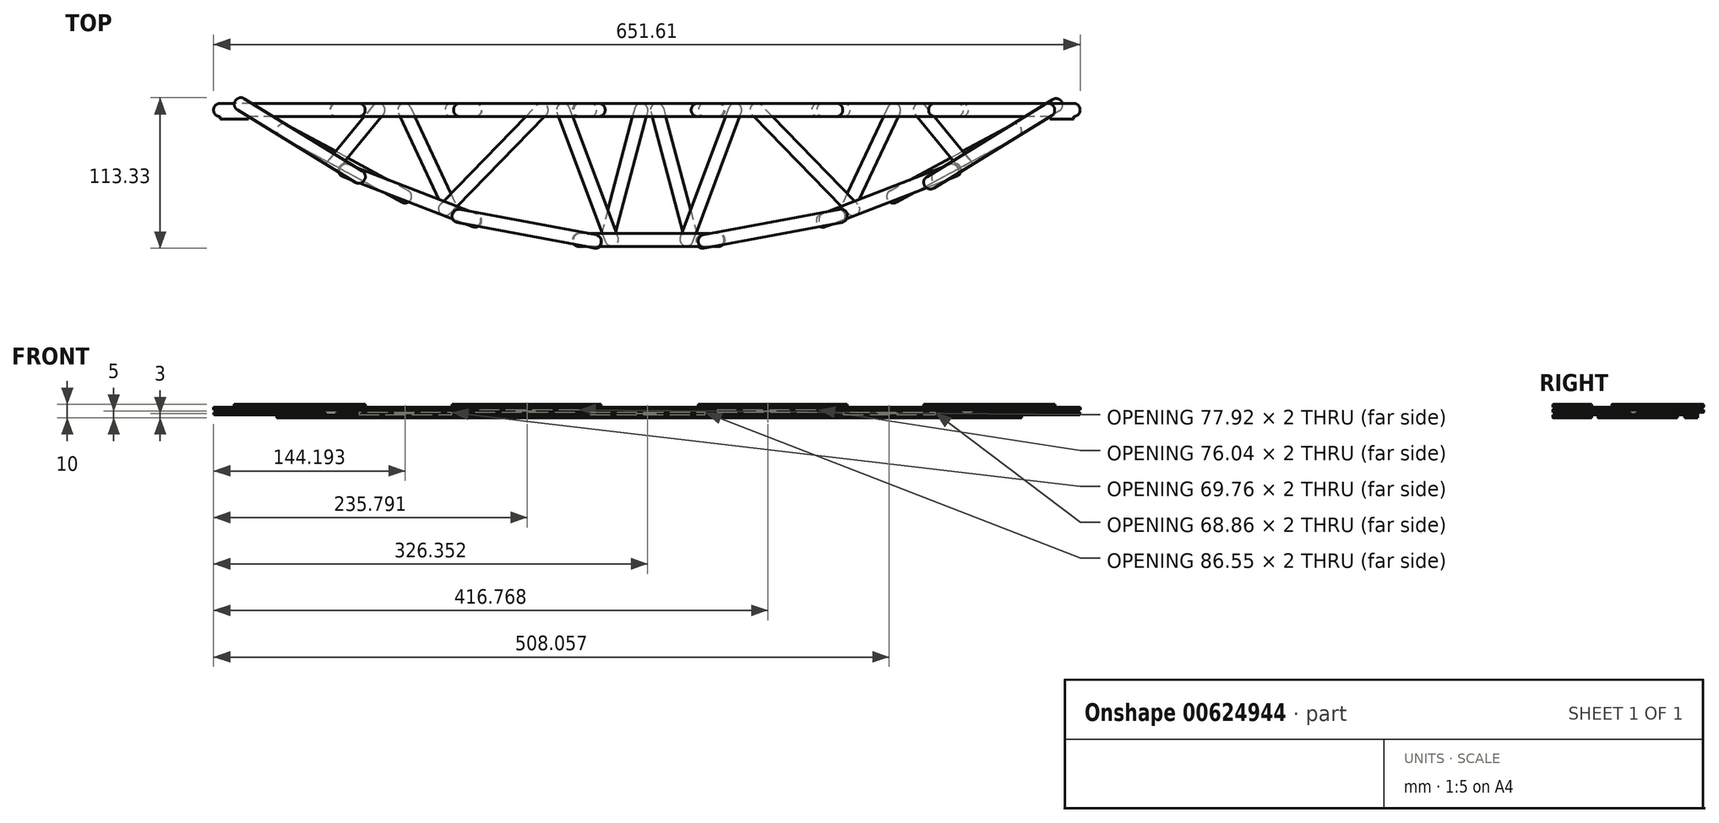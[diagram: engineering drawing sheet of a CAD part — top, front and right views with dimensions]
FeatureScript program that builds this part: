
annotation { "Feature Type Name" : "Feature", "Feature Type Description" : "" }
export const myFeature = defineFeature(function(context is Context, id is Id, definition is map)
    precondition{}
    {
        {
            var Q0;
            Q0=qCreatedBy(makeId("Top.planeOp"),FACE);
            var sketch = newSketch(context, id + "F0", { "sketchPlane" : qUnion([Q0])});
            skLineSegment(sketch, "E0", {"start": v(0, 0) * mm, "end": v(-300, 0) * mm, "construction": true});
            skLineSegment(sketch, "E1", {"start": v(0, 0) * mm, "end": v(0, -100) * mm, "construction": true});
            skLineSegment(sketch, "E2", {"start": v(0, 0) * mm, "end": v(300, 0) * mm, "construction": true});
            skArc(sketch, "E3", {"start": v(0, -100) * mm, "mid": v(158.11, -74.34) * mm, "end": v(300, 0) * mm, "construction": true});
            skArc(sketch, "E4.MirrorCS", {"start": v(0, -100) * mm, "mid": v(-158.11, -74.34) * mm, "end": v(-300, 0) * mm, "construction": true});
            skPoint(sketch, "E5", {"position": v(-222.08, -47.97) * mm});
            skPoint(sketch, "E6", {"position": v(-46.8, -97.8) * mm});
            skPoint(sketch, "E7", {"position": v(-136.73, -80.94) * mm});
            skPoint(sketch, "E8", {"position": v(46.8, -97.8) * mm});
            skPoint(sketch, "E9", {"position": v(136.73, -80.94) * mm});
            skPoint(sketch, "E10", {"position": v(222.08, -47.97) * mm});
            skLineSegment(sketch, "E11", {"start": v(-222.08, -47.97) * mm, "end": v(0, 400) * mm, "construction": true});
            skLineSegment(sketch, "E12", {"start": v(-136.73, -80.94) * mm, "end": v(0, 400) * mm, "construction": true});
            skLineSegment(sketch, "E13", {"start": v(-46.8, -97.8) * mm, "end": v(0, 400) * mm, "construction": true});
            skLineSegment(sketch, "E14", {"start": v(46.8, -97.8) * mm, "end": v(0, 400) * mm, "construction": true});
            skLineSegment(sketch, "E15", {"start": v(136.73, -80.94) * mm, "end": v(0, 400) * mm, "construction": true});
            skLineSegment(sketch, "E16", {"start": v(222.08, -47.97) * mm, "end": v(0, 400) * mm, "construction": true});
            skLineSegment(sketch, "E17", {"start": v(300, 0) * mm, "end": v(0, 400) * mm, "construction": true});
            skLineSegment(sketch, "E18", {"start": v(-300, 0) * mm, "end": v(0, 400) * mm, "construction": true});
            skSolve(sketch);
        }
        {
            var Q0;
            Q0=qCreatedBy(makeId("Top.planeOp"),FACE);
            var sketch = newSketch(context, id + "F1", { "sketchPlane" : qUnion([Q0])});
            skLineSegment(sketch, "E19", {"start": v(-220.98, -54.53) * mm, "end": v(-309.54, 0) * mm});
            skLineSegment(sketch, "E20", {"start": v(-215.73, -46) * mm, "end": v(-304.3, 8.52) * mm});
            skArc(sketch, "E21", {"start": v(-215.73, -46) * mm, "mid": v(-214.1, -52.89) * mm, "end": v(-220.98, -54.53) * mm});
            skArc(sketch, "E22", {"start": v(-304.3, 8.52) * mm, "mid": v(-311.17, 6.88) * mm, "end": v(-309.54, 0) * mm});
            skLineSegment(sketch, "E23", {"start": v(-306.92, 4.26) * mm, "end": v(-218.35, -50.27) * mm, "construction": true});
            skLineSegment(sketch, "E24", {"start": v(-132.53, -87.92) * mm, "end": v(-229.54, -50.45) * mm, "construction": true});
            skLineSegment(sketch, "E25", {"start": v(-128.93, -78.6) * mm, "end": v(-225.94, -41.12) * mm, "construction": true});
            skArc(sketch, "E26", {"start": v(-128.93, -78.6) * mm, "mid": v(-126.06, -85.06) * mm, "end": v(-132.53, -87.92) * mm, "construction": true});
            skArc(sketch, "E27", {"start": v(-225.94, -41.12) * mm, "mid": v(-232.4, -43.99) * mm, "end": v(-229.54, -50.45) * mm, "construction": true});
            skLineSegment(sketch, "E28", {"start": v(-227.74, -45.79) * mm, "end": v(-130.73, -83.26) * mm, "construction": true});
            skLineSegment(sketch, "E29", {"start": v(-42.18, -103.76) * mm, "end": v(-144.4, -84.6) * mm});
            skLineSegment(sketch, "E30", {"start": v(-40.33, -93.93) * mm, "end": v(-142.55, -74.76) * mm});
            skArc(sketch, "E31", {"start": v(-40.33, -93.93) * mm, "mid": v(-36.34, -99.77) * mm, "end": v(-42.18, -103.76) * mm});
            skArc(sketch, "E32", {"start": v(-142.55, -74.76) * mm, "mid": v(-148.39, -78.76) * mm, "end": v(-144.4, -84.6) * mm});
            skLineSegment(sketch, "E33", {"start": v(-143.48, -79.68) * mm, "end": v(-41.26, -98.84) * mm, "construction": true});
            skLineSegment(sketch, "E34", {"start": v(51.79, -102.8) * mm, "end": v(-52.21, -102.8) * mm, "construction": true});
            skLineSegment(sketch, "E35", {"start": v(51.79, -92.8) * mm, "end": v(-52.21, -92.8) * mm, "construction": true});
            skArc(sketch, "E36", {"start": v(51.79, -92.8) * mm, "mid": v(56.79, -97.8) * mm, "end": v(51.79, -102.8) * mm, "construction": true});
            skArc(sketch, "E37", {"start": v(-52.21, -92.8) * mm, "mid": v(-57.21, -97.8) * mm, "end": v(-52.21, -102.8) * mm, "construction": true});
            skLineSegment(sketch, "E38", {"start": v(-52.21, -97.8) * mm, "end": v(51.79, -97.8) * mm, "construction": true});
            skLineSegment(sketch, "E39", {"start": v(143.28, -84.8) * mm, "end": v(41.06, -103.97) * mm});
            skLineSegment(sketch, "E40", {"start": v(141.44, -74.97) * mm, "end": v(39.22, -94.14) * mm});
            skArc(sketch, "E41", {"start": v(141.44, -74.97) * mm, "mid": v(147.27, -78.97) * mm, "end": v(143.28, -84.8) * mm});
            skArc(sketch, "E42", {"start": v(39.22, -94.14) * mm, "mid": v(35.22, -99.97) * mm, "end": v(41.06, -103.97) * mm});
            skLineSegment(sketch, "E43", {"start": v(40.14, -99.05) * mm, "end": v(142.36, -79.89) * mm, "construction": true});
            skLineSegment(sketch, "E44", {"start": v(230.15, -50.22) * mm, "end": v(133.14, -87.69) * mm, "construction": true});
            skLineSegment(sketch, "E45", {"start": v(226.55, -40.89) * mm, "end": v(129.53, -78.36) * mm, "construction": true});
            skArc(sketch, "E46", {"start": v(226.55, -40.89) * mm, "mid": v(233.01, -43.75) * mm, "end": v(230.15, -50.22) * mm, "construction": true});
            skArc(sketch, "E47", {"start": v(129.53, -78.36) * mm, "mid": v(126.67, -84.83) * mm, "end": v(133.14, -87.69) * mm, "construction": true});
            skLineSegment(sketch, "E48", {"start": v(131.34, -83.03) * mm, "end": v(228.35, -45.55) * mm, "construction": true});
            skLineSegment(sketch, "E49", {"start": v(308.52, -0.62) * mm, "end": v(219.96, -55.15) * mm});
            skLineSegment(sketch, "E50", {"start": v(303.28, 7.9) * mm, "end": v(214.72, -46.63) * mm});
            skArc(sketch, "E51", {"start": v(303.28, 7.9) * mm, "mid": v(310.16, 6.25) * mm, "end": v(308.52, -0.62) * mm});
            skArc(sketch, "E52", {"start": v(214.72, -46.63) * mm, "mid": v(213.08, -53.51) * mm, "end": v(219.96, -55.15) * mm});
            skLineSegment(sketch, "E53", {"start": v(217.34, -50.9) * mm, "end": v(305.9, 3.63) * mm, "construction": true});
            skSolve(sketch);
        }
        {
            var Q0;
            Q0 = qSketchRegion(id + "F1", true);
            var Q1;
            Q1=sQuery(id+"F1.wireOp",EDGE,"E37");
            var Q2;
            Q2=sQuery(id+"F1.wireOp",EDGE,"E35");
            var Q3;
            Q3=sQuery(id+"F1.wireOp",EDGE,"E34");
            var Q4;
            Q4=sQuery(id+"F1.wireOp",EDGE,"E36");
            var Q5;
            Q5=sQuery(id+"F1.wireOp",EDGE,"E47");
            var Q6;
            Q6=sQuery(id+"F1.wireOp",EDGE,"E45");
            var Q7;
            Q7=sQuery(id+"F1.wireOp",EDGE,"E44");
            var Q8;
            Q8=sQuery(id+"F1.wireOp",EDGE,"E46");
            extrude(context, id + "F2", {"entities" : qUnion([Q0]), "surfaceEntities" : qUnion([Q1, Q2, Q3, Q4, Q5, Q6, Q7, Q8]), "depth" : 2 * mm, "offsetDistance" : 25 * mm});
        }
        {
            var Q0;
            Q0=qCreatedBy(makeId("Top.planeOp"),FACE);
            var sketch = newSketch(context, id + "F3", { "sketchPlane" : qUnion([Q0])});
            skLineSegment(sketch, "E54", {"start": v(-132.65, -87.88) * mm, "end": v(-229.66, -50.4) * mm});
            skLineSegment(sketch, "E55", {"start": v(-129.05, -78.55) * mm, "end": v(-226.06, -41.08) * mm});
            skArc(sketch, "E56", {"start": v(-129.05, -78.55) * mm, "mid": v(-126.18, -85.01) * mm, "end": v(-132.65, -87.88) * mm});
            skArc(sketch, "E57", {"start": v(-226.06, -41.08) * mm, "mid": v(-232.53, -43.94) * mm, "end": v(-229.66, -50.4) * mm});
            skLineSegment(sketch, "E58", {"start": v(-227.86, -45.74) * mm, "end": v(-130.85, -83.21) * mm, "construction": true});
            skLineSegment(sketch, "E59", {"start": v(52.07, -102.8) * mm, "end": v(-51.93, -102.8) * mm});
            skLineSegment(sketch, "E60", {"start": v(52.07, -92.8) * mm, "end": v(-51.93, -92.8) * mm});
            skArc(sketch, "E61", {"start": v(52.07, -92.8) * mm, "mid": v(57.07, -97.8) * mm, "end": v(52.07, -102.8) * mm});
            skArc(sketch, "E62", {"start": v(-51.93, -92.8) * mm, "mid": v(-56.93, -97.8) * mm, "end": v(-51.93, -102.8) * mm});
            skLineSegment(sketch, "E63", {"start": v(-51.93, -97.8) * mm, "end": v(52.07, -97.8) * mm, "construction": true});
            skLineSegment(sketch, "E64", {"start": v(229.43, -50.5) * mm, "end": v(132.42, -87.97) * mm});
            skLineSegment(sketch, "E65", {"start": v(225.83, -41.17) * mm, "end": v(128.81, -78.64) * mm});
            skArc(sketch, "E66", {"start": v(225.83, -41.17) * mm, "mid": v(232.3, -44.03) * mm, "end": v(229.43, -50.5) * mm});
            skArc(sketch, "E67", {"start": v(128.81, -78.64) * mm, "mid": v(125.95, -85.1) * mm, "end": v(132.42, -87.97) * mm});
            skLineSegment(sketch, "E68", {"start": v(130.62, -83.3) * mm, "end": v(227.63, -45.83) * mm, "construction": true});
            skLineSegment(sketch, "E69", {"start": v(-218.23, -5) * mm, "end": v(-322.23, -5) * mm});
            skLineSegment(sketch, "E70", {"start": v(-218.23, 5) * mm, "end": v(-322.23, 5) * mm});
            skArc(sketch, "E71", {"start": v(-218.23, 5) * mm, "mid": v(-213.23, 0) * mm, "end": v(-218.23, -5) * mm});
            skArc(sketch, "E72", {"start": v(-322.23, 5) * mm, "mid": v(-327.23, 0) * mm, "end": v(-322.23, -5) * mm});
            skLineSegment(sketch, "E73", {"start": v(-322.23, 0) * mm, "end": v(-218.23, 0) * mm, "construction": true});
            skPoint(sketch, "E74", {"position": v(-301.42, -5) * mm});
            skLineSegment(sketch, "E75", {"start": v(-129.86, -5) * mm, "end": v(-233.86, -5) * mm, "construction": true});
            skLineSegment(sketch, "E76", {"start": v(-129.86, 5) * mm, "end": v(-233.86, 5) * mm, "construction": true});
            skArc(sketch, "E77", {"start": v(-129.86, 5) * mm, "mid": v(-124.86, 0) * mm, "end": v(-129.86, -5) * mm, "construction": true});
            skArc(sketch, "E78", {"start": v(-233.86, 5) * mm, "mid": v(-238.86, 0) * mm, "end": v(-233.86, -5) * mm, "construction": true});
            skLineSegment(sketch, "E79", {"start": v(-233.86, 0) * mm, "end": v(-129.86, 0) * mm, "construction": true});
            skLineSegment(sketch, "E80", {"start": v(-44.46, -5) * mm, "end": v(-148.46, -5) * mm});
            skLineSegment(sketch, "E81", {"start": v(-44.46, 5) * mm, "end": v(-148.46, 5) * mm});
            skArc(sketch, "E82", {"start": v(-44.46, 5) * mm, "mid": v(-39.46, 0) * mm, "end": v(-44.46, -5) * mm});
            skArc(sketch, "E83", {"start": v(-148.46, 5) * mm, "mid": v(-153.46, 0) * mm, "end": v(-148.46, -5) * mm});
            skLineSegment(sketch, "E84", {"start": v(-148.46, 0) * mm, "end": v(-44.46, 0) * mm, "construction": true});
            skLineSegment(sketch, "E85", {"start": v(50.88, -5) * mm, "end": v(-53.12, -5) * mm, "construction": true});
            skLineSegment(sketch, "E86", {"start": v(50.88, 5) * mm, "end": v(-53.12, 5) * mm, "construction": true});
            skArc(sketch, "E87", {"start": v(50.88, 5) * mm, "mid": v(55.88, 0) * mm, "end": v(50.88, -5) * mm, "construction": true});
            skArc(sketch, "E88", {"start": v(-53.12, 5) * mm, "mid": v(-58.12, 0) * mm, "end": v(-53.12, -5) * mm, "construction": true});
            skLineSegment(sketch, "E89", {"start": v(-53.12, 0) * mm, "end": v(50.88, 0) * mm, "construction": true});
            skLineSegment(sketch, "E90", {"start": v(146.09, -5) * mm, "end": v(42.09, -5) * mm});
            skLineSegment(sketch, "E91", {"start": v(146.09, 5) * mm, "end": v(42.09, 5) * mm});
            skArc(sketch, "E92", {"start": v(146.09, 5) * mm, "mid": v(151.09, 0) * mm, "end": v(146.09, -5) * mm});
            skArc(sketch, "E93", {"start": v(42.09, 5) * mm, "mid": v(37.09, 0) * mm, "end": v(42.09, -5) * mm});
            skLineSegment(sketch, "E94", {"start": v(42.09, 0) * mm, "end": v(146.09, 0) * mm, "construction": true});
            skLineSegment(sketch, "E95", {"start": v(229.8, -5) * mm, "end": v(125.8, -5) * mm, "construction": true});
            skLineSegment(sketch, "E96", {"start": v(229.8, 5) * mm, "end": v(125.8, 5) * mm, "construction": true});
            skArc(sketch, "E97", {"start": v(229.8, 5) * mm, "mid": v(234.8, 0) * mm, "end": v(229.8, -5) * mm, "construction": true});
            skArc(sketch, "E98", {"start": v(125.8, 5) * mm, "mid": v(120.8, 0) * mm, "end": v(125.8, -5) * mm, "construction": true});
            skLineSegment(sketch, "E99", {"start": v(125.8, 0) * mm, "end": v(229.8, 0) * mm, "construction": true});
            skLineSegment(sketch, "E100", {"start": v(318.95, -5) * mm, "end": v(214.95, -5) * mm});
            skLineSegment(sketch, "E101", {"start": v(318.95, 5) * mm, "end": v(214.95, 5) * mm});
            skArc(sketch, "E102", {"start": v(318.95, 5) * mm, "mid": v(323.95, 0) * mm, "end": v(318.95, -5) * mm});
            skArc(sketch, "E103", {"start": v(214.95, 5) * mm, "mid": v(209.95, 0) * mm, "end": v(214.95, -5) * mm});
            skLineSegment(sketch, "E104", {"start": v(214.95, 0) * mm, "end": v(318.95, 0) * mm, "construction": true});
            skSolve(sketch);
        }
        {
            var Q0;
            Q0 = qSketchRegion(id + "F3", true);
            extrude(context, id + "F4", {"entities" : qUnion([Q0]), "operationType" : NewBodyOperationType.ADD, "oppositeDirection" : true, "depth" : 2 * mm, "offsetDistance" : 25 * mm});
        }
        {
            var Q0;
            Q0=qCreatedBy(makeId("Top.planeOp"),FACE);
            var sketch = newSketch(context, id + "F5", { "sketchPlane" : qUnion([Q0])});
            skLineSegment(sketch, "E105", {"start": v(-130.7, -5) * mm, "end": v(-234.7, -5) * mm});
            skLineSegment(sketch, "E106", {"start": v(-130.7, 5) * mm, "end": v(-234.7, 5) * mm});
            skArc(sketch, "E107", {"start": v(-130.7, 5) * mm, "mid": v(-125.7, 0) * mm, "end": v(-130.7, -5) * mm});
            skArc(sketch, "E108", {"start": v(-234.7, 5) * mm, "mid": v(-239.7, 0) * mm, "end": v(-234.7, -5) * mm});
            skLineSegment(sketch, "E109", {"start": v(-234.7, 0) * mm, "end": v(-130.7, 0) * mm, "construction": true});
            skLineSegment(sketch, "E110", {"start": v(51.21, -5) * mm, "end": v(-52.79, -5) * mm});
            skLineSegment(sketch, "E111", {"start": v(51.21, 5) * mm, "end": v(-52.79, 5) * mm});
            skArc(sketch, "E112", {"start": v(51.21, 5) * mm, "mid": v(56.21, 0) * mm, "end": v(51.21, -5) * mm});
            skArc(sketch, "E113", {"start": v(-52.79, 5) * mm, "mid": v(-57.79, 0) * mm, "end": v(-52.79, -5) * mm});
            skLineSegment(sketch, "E114", {"start": v(-52.79, 0) * mm, "end": v(51.21, 0) * mm, "construction": true});
            skLineSegment(sketch, "E115", {"start": v(231.25, -5) * mm, "end": v(127.25, -5) * mm});
            skLineSegment(sketch, "E116", {"start": v(231.25, 5) * mm, "end": v(127.25, 5) * mm});
            skArc(sketch, "E117", {"start": v(231.25, 5) * mm, "mid": v(236.25, 0) * mm, "end": v(231.25, -5) * mm});
            skArc(sketch, "E118", {"start": v(127.25, 5) * mm, "mid": v(122.25, 0) * mm, "end": v(127.25, -5) * mm});
            skLineSegment(sketch, "E119", {"start": v(127.25, 0) * mm, "end": v(231.25, 0) * mm, "construction": true});
            skSolve(sketch);
        }
        {
            var Q0;
            Q0 = qSketchRegion(id + "F5", true);
            extrude(context, id + "F6", {"entities" : qUnion([Q0]), "operationType" : NewBodyOperationType.ADD, "depth" : 2 * mm, "offsetDistance" : 25 * mm});
        }
        {
            var Q0;
            {var subQ3=sQuery(id+"F3.wireOp",EDGE,"E60");var subQ4=sQuery(id+"F1.wireOp",EDGE,"E30");var subQ5=sQuery(id+"F3.wireOp",EDGE,"E59");Q0=makeQuery(id+"F4.boolean.opBoolean","SPLIT",FACE,{"disambiguationData":[TD([makeQuery(id+"F2.opExtrude","SWEPT_FACE",FACE,{"disambiguationData":[OSD([subQ4])]})])],"derivedFrom":makeQuery(id+"F4.opExtrude","CAP_FACE",FACE,{"disambiguationData":[OSD([subQ5,subQ3,sQuery(id+"F3.wireOp",EDGE,"E61"),sQuery(id+"F3.wireOp",EDGE,"E62")])],"isStart":true})});}
            var sketch = newSketch(context, id + "F7", { "sketchPlane" : qUnion([Q0])});
            skLineSegment(sketch, "E120", {"start": v(-32.8, -99.15) * mm, "end": v(-69.28, -1.75) * mm});
            skLineSegment(sketch, "E121", {"start": v(-23.44, -95.64) * mm, "end": v(-59.92, 1.75) * mm});
            skArc(sketch, "E122", {"start": v(-23.44, -95.64) * mm, "mid": v(-26.37, -102.07) * mm, "end": v(-32.8, -99.15) * mm});
            skArc(sketch, "E123", {"start": v(-59.92, 1.75) * mm, "mid": v(-66.35, 4.68) * mm, "end": v(-69.28, -1.75) * mm});
            skLineSegment(sketch, "E124", {"start": v(-64.6, 0) * mm, "end": v(-28.12, -97.4) * mm, "construction": true});
            skLineSegment(sketch, "E125", {"start": v(-157, -71) * mm, "end": v(-84.43, 3.49) * mm});
            skLineSegment(sketch, "E126", {"start": v(-149.84, -77.98) * mm, "end": v(-77.27, -3.49) * mm});
            skArc(sketch, "E127", {"start": v(-149.84, -77.98) * mm, "mid": v(-156.9, -78.08) * mm, "end": v(-157, -71) * mm});
            skArc(sketch, "E128", {"start": v(-77.27, -3.49) * mm, "mid": v(-77.36, 3.58) * mm, "end": v(-84.43, 3.49) * mm});
            skLineSegment(sketch, "E129", {"start": v(-80.85, 0) * mm, "end": v(-153.42, -74.5) * mm, "construction": true});
            skArc(sketch, "E130.MirrorCS", {"start": v(59.92, 1.75) * mm, "mid": v(66.35, 4.68) * mm, "end": v(69.28, -1.75) * mm});
            skLineSegment(sketch, "E131.MirrorCS", {"start": v(23.44, -95.64) * mm, "end": v(59.92, 1.75) * mm});
            skLineSegment(sketch, "E132.MirrorCS", {"start": v(32.8, -99.15) * mm, "end": v(69.28, -1.75) * mm});
            skArc(sketch, "E133.MirrorCS", {"start": v(23.44, -95.64) * mm, "mid": v(26.37, -102.07) * mm, "end": v(32.8, -99.15) * mm});
            skLineSegment(sketch, "E134.MirrorCS", {"start": v(149.84, -77.98) * mm, "end": v(77.27, -3.49) * mm});
            skLineSegment(sketch, "E135.MirrorCS", {"start": v(157, -71) * mm, "end": v(84.43, 3.49) * mm});
            skArc(sketch, "E136.MirrorCS", {"start": v(77.27, -3.49) * mm, "mid": v(77.36, 3.58) * mm, "end": v(84.43, 3.49) * mm});
            skArc(sketch, "E137.MirrorCS", {"start": v(149.84, -77.98) * mm, "mid": v(156.9, -78.08) * mm, "end": v(157, -71) * mm});
            skSolve(sketch);
        }
        {
            var Q0;
            Q0 = qSketchRegion(id + "F7", true);
            extrude(context, id + "F8", {"entities" : qUnion([Q0]), "operationType" : NewBodyOperationType.ADD, "depth" : 2 * mm, "offsetDistance" : 25 * mm});
        }
        {
            var Q0;
            Q0=makeQuery(id+"F6.opExtrude","CAP_FACE",FACE,{"disambiguationData":[OSD([sQuery(id+"F5.wireOp",EDGE,"E105"),sQuery(id+"F5.wireOp",EDGE,"E106"),sQuery(id+"F5.wireOp",EDGE,"E107"),sQuery(id+"F5.wireOp",EDGE,"E108")])],"isStart":true});
            var sketch = newSketch(context, id + "F9", { "sketchPlane" : qUnion([Q0])});
            skLineSegment(sketch, "E138", {"start": v(-188.56, 2.12) * mm, "end": v(-157.99, 67.37) * mm});
            skLineSegment(sketch, "E139", {"start": v(-179.5, -2.12) * mm, "end": v(-144.5, 72.58) * mm});
            skArc(sketch, "E140", {"start": v(-179.5, -2.12) * mm, "mid": v(-186.15, -4.53) * mm, "end": v(-188.56, 2.12) * mm});
            skLineSegment(sketch, "E141", {"start": v(-148.56, 75.71) * mm, "end": v(-184.03, 0) * mm, "construction": true});
            skLineSegment(sketch, "E142", {"start": v(-207.49, -3.17) * mm, "end": v(-243.5, 40.66) * mm});
            skLineSegment(sketch, "E143", {"start": v(-199.76, 3.17) * mm, "end": v(-234.9, 45.95) * mm});
            skArc(sketch, "E144", {"start": v(-199.76, 3.17) * mm, "mid": v(-200.45, -3.86) * mm, "end": v(-207.49, -3.17) * mm});
            skLineSegment(sketch, "E145", {"start": v(-242.92, 47.84) * mm, "end": v(-203.63, 0) * mm, "construction": true});
            skArc(sketch, "E146.MirrorCS", {"start": v(179.5, -2.12) * mm, "mid": v(186.15, -4.53) * mm, "end": v(188.56, 2.12) * mm});
            skArc(sketch, "E147.MirrorCS", {"start": v(199.76, 3.17) * mm, "mid": v(200.45, -3.86) * mm, "end": v(207.49, -3.17) * mm});
            skLineSegment(sketch, "E148.MirrorCS", {"start": v(188.56, 2.12) * mm, "end": v(157.99, 67.37) * mm});
            skLineSegment(sketch, "E149.MirrorCS", {"start": v(242.92, 47.84) * mm, "end": v(203.63, 0) * mm, "construction": true});
            skLineSegment(sketch, "E150.MirrorCS", {"start": v(179.5, -2.12) * mm, "end": v(144.5, 72.58) * mm});
            skLineSegment(sketch, "E151.MirrorCS", {"start": v(148.56, 75.71) * mm, "end": v(184.03, 0) * mm, "construction": true});
            skLineSegment(sketch, "E152.MirrorCS", {"start": v(207.49, -3.17) * mm, "end": v(243.5, 40.66) * mm});
            skLineSegment(sketch, "E153.MirrorCS", {"start": v(199.76, 3.17) * mm, "end": v(234.9, 45.95) * mm});
            skLineSegment(sketch, "E154", {"start": v(-157.99, 67.37) * mm, "end": v(-144.5, 72.58) * mm});
            skLineSegment(sketch, "E155", {"start": v(-234.9, 45.95) * mm, "end": v(-243.5, 40.66) * mm});
            skLineSegment(sketch, "E156.MirrorCS", {"start": v(157.99, 67.37) * mm, "end": v(144.5, 72.58) * mm});
            skLineSegment(sketch, "E157.MirrorCS", {"start": v(234.9, 45.95) * mm, "end": v(243.5, 40.66) * mm});
            skLineSegment(sketch, "E158", {"start": v(-10.83, -1.28) * mm, "end": v(-35.8, 92.8) * mm});
            skLineSegment(sketch, "E159", {"start": v(-1.17, 1.28) * mm, "end": v(-25.45, 92.8) * mm});
            skArc(sketch, "E160", {"start": v(-1.17, 1.28) * mm, "mid": v(-4.72, -4.83) * mm, "end": v(-10.83, -1.28) * mm});
            skLineSegment(sketch, "E161", {"start": v(-32.6, 100.24) * mm, "end": v(-6, 0) * mm, "construction": true});
            skLineSegment(sketch, "E162", {"start": v(-25.45, 92.8) * mm, "end": v(-35.8, 92.8) * mm});
            skLineSegment(sketch, "E163.MirrorCS", {"start": v(25.45, 92.8) * mm, "end": v(35.8, 92.8) * mm});
            skLineSegment(sketch, "E164.MirrorCS", {"start": v(10.83, -1.28) * mm, "end": v(35.8, 92.8) * mm});
            skLineSegment(sketch, "E165.MirrorCS", {"start": v(1.17, 1.28) * mm, "end": v(25.45, 92.8) * mm});
            skArc(sketch, "E166.MirrorCS", {"start": v(1.17, 1.28) * mm, "mid": v(4.72, -4.83) * mm, "end": v(10.83, -1.28) * mm});
            skSolve(sketch);
        }
        {
            var Q0;
            Q0 = qSketchRegion(id + "F9", true);
            extrude(context, id + "F10", {"entities" : qUnion([Q0]), "operationType" : NewBodyOperationType.ADD, "depth" : 2 * mm, "offsetDistance" : 25 * mm});
        }
        {
            var Q0;
            Q0=makeQuery(id+"F4.opExtrude","CAP_FACE",FACE,{"disambiguationData":[OSD([sQuery(id+"F3.wireOp",EDGE,"E80"),sQuery(id+"F3.wireOp",EDGE,"E81"),sQuery(id+"F3.wireOp",EDGE,"E82"),sQuery(id+"F3.wireOp",EDGE,"E83")])],"isStart":false});
            var sketch = newSketch(context, id + "F11", { "sketchPlane" : qUnion([Q0])});
            skLineSegment(sketch, "E167", {"start": v(52.2, -5) * mm, "end": v(-51.8, -5) * mm});
            skLineSegment(sketch, "E168", {"start": v(52.2, 5) * mm, "end": v(-51.8, 5) * mm});
            skArc(sketch, "E169", {"start": v(52.2, 5) * mm, "mid": v(57.2, 0) * mm, "end": v(52.2, -5) * mm});
            skArc(sketch, "E170", {"start": v(-51.8, 5) * mm, "mid": v(-56.8, 0) * mm, "end": v(-51.8, -5) * mm});
            skLineSegment(sketch, "E171", {"start": v(-51.8, 0) * mm, "end": v(52.2, 0) * mm, "construction": true});
            skLineSegment(sketch, "E172", {"start": v(-131.03, -5) * mm, "end": v(-235.03, -5) * mm});
            skLineSegment(sketch, "E173", {"start": v(-131.03, 5) * mm, "end": v(-235.03, 5) * mm});
            skArc(sketch, "E174", {"start": v(-131.03, 5) * mm, "mid": v(-126.03, 0) * mm, "end": v(-131.03, -5) * mm});
            skArc(sketch, "E175", {"start": v(-235.03, 5) * mm, "mid": v(-240.03, 0) * mm, "end": v(-235.03, -5) * mm});
            skLineSegment(sketch, "E176", {"start": v(-235.03, 0) * mm, "end": v(-131.03, 0) * mm, "construction": true});
            skPoint(sketch, "E177", {"position": v(-56.8, 0) * mm});
            skLineSegment(sketch, "E178", {"start": v(-39.26, 94.13) * mm, "end": v(-141.48, 74.96) * mm});
            skLineSegment(sketch, "E179", {"start": v(-41.1, 103.96) * mm, "end": v(-143.32, 84.8) * mm});
            skArc(sketch, "E180", {"start": v(-41.1, 103.96) * mm, "mid": v(-35.26, 99.97) * mm, "end": v(-39.26, 94.13) * mm});
            skArc(sketch, "E181", {"start": v(-143.32, 84.8) * mm, "mid": v(-147.31, 78.96) * mm, "end": v(-141.48, 74.96) * mm});
            skLineSegment(sketch, "E182", {"start": v(-142.4, 79.88) * mm, "end": v(-40.18, 99.05) * mm, "construction": true});
            skLineSegment(sketch, "E183", {"start": v(-181.2, 60.68) * mm, "end": v(-272.59, 11.02) * mm});
            skLineSegment(sketch, "E184", {"start": v(-185.98, 69.47) * mm, "end": v(-277.36, 19.8) * mm});
            skArc(sketch, "E185", {"start": v(-185.98, 69.47) * mm, "mid": v(-179.2, 67.46) * mm, "end": v(-181.2, 60.68) * mm});
            skArc(sketch, "E186", {"start": v(-277.36, 19.8) * mm, "mid": v(-279.37, 13.03) * mm, "end": v(-272.59, 11.02) * mm});
            skLineSegment(sketch, "E187", {"start": v(-274.98, 15.42) * mm, "end": v(-183.6, 65.07) * mm, "construction": true});
            skArc(sketch, "E188.MirrorCS", {"start": v(41.1, 103.96) * mm, "mid": v(35.26, 99.97) * mm, "end": v(39.26, 94.13) * mm});
            skLineSegment(sketch, "E189.MirrorCS", {"start": v(39.26, 94.13) * mm, "end": v(141.48, 74.96) * mm});
            skLineSegment(sketch, "E190.MirrorCS", {"start": v(41.1, 103.96) * mm, "end": v(143.32, 84.8) * mm});
            skLineSegment(sketch, "E191.MirrorCS", {"start": v(142.4, 79.88) * mm, "end": v(40.18, 99.05) * mm, "construction": true});
            skArc(sketch, "E192.MirrorCS", {"start": v(131.03, 5) * mm, "mid": v(126.03, 0) * mm, "end": v(131.03, -5) * mm});
            skArc(sketch, "E193.MirrorCS", {"start": v(143.32, 84.8) * mm, "mid": v(147.31, 78.96) * mm, "end": v(141.48, 74.96) * mm});
            skArc(sketch, "E194.MirrorCS", {"start": v(235.03, 5) * mm, "mid": v(240.03, 0) * mm, "end": v(235.03, -5) * mm});
            skArc(sketch, "E195.MirrorCS", {"start": v(185.98, 69.47) * mm, "mid": v(179.2, 67.46) * mm, "end": v(181.2, 60.68) * mm});
            skArc(sketch, "E196.MirrorCS", {"start": v(277.36, 19.8) * mm, "mid": v(279.37, 13.03) * mm, "end": v(272.59, 11.02) * mm});
            skLineSegment(sketch, "E197.MirrorCS", {"start": v(235.03, 0) * mm, "end": v(131.03, 0) * mm, "construction": true});
            skLineSegment(sketch, "E198.MirrorCS", {"start": v(274.98, 15.42) * mm, "end": v(183.6, 65.07) * mm, "construction": true});
            skLineSegment(sketch, "E199.MirrorCS", {"start": v(185.98, 69.47) * mm, "end": v(277.36, 19.8) * mm});
            skLineSegment(sketch, "E200.MirrorCS", {"start": v(181.2, 60.68) * mm, "end": v(272.59, 11.02) * mm});
            skLineSegment(sketch, "E201.MirrorCS", {"start": v(131.03, -5) * mm, "end": v(235.03, -5) * mm});
            skLineSegment(sketch, "E202.MirrorCS", {"start": v(131.03, 5) * mm, "end": v(235.03, 5) * mm});
            skSolve(sketch);
        }
        {
            var Q0;
            Q0 = qSketchRegion(id + "F11", true);
            extrude(context, id + "F12", {"entities" : qUnion([Q0]), "operationType" : NewBodyOperationType.ADD, "depth" : 2 * mm, "offsetDistance" : 25 * mm});
        }
        {
            var Q0;
            Q0=makeQuery(id+"F2.opExtrude","CAP_FACE",FACE,{"disambiguationData":[OSD([sQuery(id+"F1.wireOp",EDGE,"E19"),sQuery(id+"F1.wireOp",EDGE,"E20"),sQuery(id+"F1.wireOp",EDGE,"E21"),sQuery(id+"F1.wireOp",EDGE,"E22")])],"isStart":false});
            var sketch = newSketch(context, id + "F13", { "sketchPlane" : qUnion([Q0])});
            skLineSegment(sketch, "E203", {"start": v(-133.4, -87.59) * mm, "end": v(-230.41, -50.11) * mm});
            skLineSegment(sketch, "E204", {"start": v(-129.8, -78.26) * mm, "end": v(-226.81, -40.79) * mm});
            skArc(sketch, "E205", {"start": v(-226.81, -40.79) * mm, "mid": v(-233.28, -43.65) * mm, "end": v(-230.41, -50.11) * mm});
            skLineSegment(sketch, "E206", {"start": v(-228.61, -45.45) * mm, "end": v(-131.6, -82.92) * mm, "construction": true});
            skArc(sketch, "E207", {"start": v(-129.8, -78.26) * mm, "mid": v(-126.93, -84.73) * mm, "end": v(-133.4, -87.59) * mm});
            skLineSegment(sketch, "E208", {"start": v(231.45, -49.71) * mm, "end": v(134.43, -87.19) * mm});
            skLineSegment(sketch, "E209", {"start": v(227.85, -40.39) * mm, "end": v(130.83, -77.86) * mm});
            skArc(sketch, "E210", {"start": v(227.85, -40.39) * mm, "mid": v(234.31, -43.25) * mm, "end": v(231.45, -49.71) * mm});
            skArc(sketch, "E211", {"start": v(130.83, -77.86) * mm, "mid": v(127.97, -84.33) * mm, "end": v(134.43, -87.19) * mm});
            skLineSegment(sketch, "E212", {"start": v(132.63, -82.52) * mm, "end": v(229.65, -45.05) * mm, "construction": true});
            skLineSegment(sketch, "E213", {"start": v(51.34, -102.8) * mm, "end": v(-52.66, -102.8) * mm});
            skLineSegment(sketch, "E214", {"start": v(51.34, -92.8) * mm, "end": v(-52.66, -92.8) * mm});
            skArc(sketch, "E215", {"start": v(51.34, -92.8) * mm, "mid": v(56.34, -97.8) * mm, "end": v(51.34, -102.8) * mm});
            skArc(sketch, "E216", {"start": v(-52.66, -92.8) * mm, "mid": v(-57.66, -97.8) * mm, "end": v(-52.66, -102.8) * mm});
            skLineSegment(sketch, "E217", {"start": v(-52.66, -97.8) * mm, "end": v(51.34, -97.8) * mm, "construction": true});
            skLineSegment(sketch, "E218", {"start": v(319.07, -5) * mm, "end": v(215.07, -5) * mm});
            skLineSegment(sketch, "E219", {"start": v(319.07, 5) * mm, "end": v(215.07, 5) * mm});
            skArc(sketch, "E220", {"start": v(319.07, 5) * mm, "mid": v(324.07, 0) * mm, "end": v(319.07, -5) * mm});
            skArc(sketch, "E221", {"start": v(215.07, 5) * mm, "mid": v(210.07, 0) * mm, "end": v(215.07, -5) * mm});
            skLineSegment(sketch, "E222", {"start": v(215.07, 0) * mm, "end": v(319.07, 0) * mm, "construction": true});
            skLineSegment(sketch, "E223", {"start": v(140.56, -5) * mm, "end": v(36.56, -5) * mm});
            skLineSegment(sketch, "E224", {"start": v(140.56, 5) * mm, "end": v(36.56, 5) * mm});
            skArc(sketch, "E225", {"start": v(140.56, 5) * mm, "mid": v(145.56, 0) * mm, "end": v(140.56, -5) * mm});
            skArc(sketch, "E226", {"start": v(36.56, 5) * mm, "mid": v(31.56, 0) * mm, "end": v(36.56, -5) * mm});
            skLineSegment(sketch, "E227", {"start": v(36.56, 0) * mm, "end": v(140.56, 0) * mm, "construction": true});
            skLineSegment(sketch, "E228", {"start": v(-38.04, -5) * mm, "end": v(-142.04, -5) * mm});
            skLineSegment(sketch, "E229", {"start": v(-38.04, 5) * mm, "end": v(-142.04, 5) * mm});
            skArc(sketch, "E230", {"start": v(-38.04, 5) * mm, "mid": v(-33.04, 0) * mm, "end": v(-38.04, -5) * mm});
            skArc(sketch, "E231", {"start": v(-142.04, 5) * mm, "mid": v(-147.04, 0) * mm, "end": v(-142.04, -5) * mm});
            skLineSegment(sketch, "E232", {"start": v(-142.04, 0) * mm, "end": v(-38.04, 0) * mm, "construction": true});
            skLineSegment(sketch, "E233", {"start": v(-218.54, -5) * mm, "end": v(-322.54, -5) * mm});
            skLineSegment(sketch, "E234", {"start": v(-218.54, 5) * mm, "end": v(-322.54, 5) * mm});
            skArc(sketch, "E235", {"start": v(-218.54, 5) * mm, "mid": v(-213.54, 0) * mm, "end": v(-218.54, -5) * mm});
            skArc(sketch, "E236", {"start": v(-322.54, 5) * mm, "mid": v(-327.54, 0) * mm, "end": v(-322.54, -5) * mm});
            skLineSegment(sketch, "E237", {"start": v(-322.54, 0) * mm, "end": v(-218.54, 0) * mm, "construction": true});
            skSolve(sketch);
        }
        {
            var Q0;
            Q0 = qSketchRegion(id + "F13", true);
            extrude(context, id + "F14", {"entities" : qUnion([Q0]), "operationType" : NewBodyOperationType.ADD, "depth" : 2 * mm, "offsetDistance" : 25 * mm});
        }
        {
            var Q0;
            Q0=makeQuery(id+"F14.opExtrude","CAP_FACE",FACE,{"disambiguationData":[OSD([sQuery(id+"F13.wireOp",EDGE,"E218"),sQuery(id+"F13.wireOp",EDGE,"E219"),sQuery(id+"F13.wireOp",EDGE,"E220"),sQuery(id+"F13.wireOp",EDGE,"E221")])],"isStart":false});
            var sketch = newSketch(context, id + "F15", { "sketchPlane" : qUnion([Q0])});
            skLineSegment(sketch, "E238", {"start": v(302.62, -4.26) * mm, "end": v(214.06, -58.78) * mm});
            skLineSegment(sketch, "E239", {"start": v(297.38, 4.26) * mm, "end": v(208.82, -50.27) * mm});
            skArc(sketch, "E240", {"start": v(297.38, 4.26) * mm, "mid": v(304.26, 2.62) * mm, "end": v(302.62, -4.26) * mm});
            skArc(sketch, "E241", {"start": v(208.82, -50.27) * mm, "mid": v(207.18, -57.15) * mm, "end": v(214.06, -58.78) * mm});
            skLineSegment(sketch, "E242", {"start": v(211.44, -54.53) * mm, "end": v(300, 0) * mm, "construction": true});
            skLineSegment(sketch, "E243", {"start": v(-221, -54.5) * mm, "end": v(-309.57, 0.02) * mm});
            skLineSegment(sketch, "E244", {"start": v(-215.77, -45.99) * mm, "end": v(-304.33, 8.54) * mm});
            skArc(sketch, "E245", {"start": v(-215.77, -45.99) * mm, "mid": v(-214.13, -52.87) * mm, "end": v(-221, -54.5) * mm});
            skArc(sketch, "E246", {"start": v(-304.33, 8.54) * mm, "mid": v(-311.2, 6.9) * mm, "end": v(-309.57, 0.02) * mm});
            skLineSegment(sketch, "E247", {"start": v(-306.95, 4.28) * mm, "end": v(-218.39, -50.25) * mm, "construction": true});
            skLineSegment(sketch, "E248", {"start": v(-41.92, -103.8) * mm, "end": v(-144.14, -84.64) * mm});
            skLineSegment(sketch, "E249", {"start": v(-40.08, -93.98) * mm, "end": v(-142.3, -74.81) * mm});
            skArc(sketch, "E250", {"start": v(-40.08, -93.98) * mm, "mid": v(-36.09, -99.81) * mm, "end": v(-41.92, -103.8) * mm});
            skArc(sketch, "E251", {"start": v(-142.3, -74.81) * mm, "mid": v(-148.13, -78.8) * mm, "end": v(-144.14, -84.64) * mm});
            skLineSegment(sketch, "E252", {"start": v(-143.22, -79.73) * mm, "end": v(-41, -98.9) * mm, "construction": true});
            skLineSegment(sketch, "E253", {"start": v(144.98, -84.48) * mm, "end": v(42.76, -103.65) * mm});
            skLineSegment(sketch, "E254", {"start": v(143.14, -74.65) * mm, "end": v(40.92, -93.82) * mm});
            skArc(sketch, "E255", {"start": v(143.14, -74.65) * mm, "mid": v(148.98, -78.65) * mm, "end": v(144.98, -84.48) * mm});
            skArc(sketch, "E256", {"start": v(40.92, -93.82) * mm, "mid": v(36.93, -99.66) * mm, "end": v(42.76, -103.65) * mm});
            skLineSegment(sketch, "E257", {"start": v(41.84, -98.73) * mm, "end": v(144.06, -79.57) * mm, "construction": true});
            skSolve(sketch);
        }
        {
            var Q0;
            Q0 = qSketchRegion(id + "F15", true);
            extrude(context, id + "F16", {"entities" : qUnion([Q0]), "operationType" : NewBodyOperationType.ADD, "depth" : 2 * mm, "offsetDistance" : 25 * mm});
        }
        {
            var Q0;
            Q0=makeQuery(id+"F14.boolean.opBoolean","MERGE",FACE,{"derivedFrom":[makeQuery(id+"F12.boolean.opBoolean","MERGE",FACE,{"derivedFrom":[makeQuery(id+"F6.boolean.opBoolean","MERGE",FACE,{"derivedFrom":[makeQuery(id+"F4.opExtrude","SWEPT_FACE",FACE,{"disambiguationData":[OSD([sQuery(id+"F3.wireOp",EDGE,"E69")])]}),makeQuery(id+"F4.opExtrude","SWEPT_FACE",FACE,{"disambiguationData":[OSD([sQuery(id+"F3.wireOp",EDGE,"E80")])]}),makeQuery(id+"F4.opExtrude","SWEPT_FACE",FACE,{"disambiguationData":[OSD([sQuery(id+"F3.wireOp",EDGE,"E90")])]}),makeQuery(id+"F4.opExtrude","SWEPT_FACE",FACE,{"disambiguationData":[OSD([sQuery(id+"F3.wireOp",EDGE,"E100")])]}),makeQuery(id+"F6.opExtrude","SWEPT_FACE",FACE,{"disambiguationData":[OSD([sQuery(id+"F5.wireOp",EDGE,"E105")])]}),makeQuery(id+"F6.opExtrude","SWEPT_FACE",FACE,{"disambiguationData":[OSD([sQuery(id+"F5.wireOp",EDGE,"E110")])]}),makeQuery(id+"F6.opExtrude","SWEPT_FACE",FACE,{"disambiguationData":[OSD([sQuery(id+"F5.wireOp",EDGE,"E115")])]})]}),makeQuery(id+"F12.opExtrude","SWEPT_FACE",FACE,{"disambiguationData":[OSD([sQuery(id+"F11.wireOp",EDGE,"E168")])]}),makeQuery(id+"F12.opExtrude","SWEPT_FACE",FACE,{"disambiguationData":[OSD([sQuery(id+"F11.wireOp",EDGE,"E173")])]}),makeQuery(id+"F12.opExtrude","SWEPT_FACE",FACE,{"disambiguationData":[OSD([sQuery(id+"F11.wireOp",EDGE,"E202.MirrorCS")])]})]}),makeQuery(id+"F14.opExtrude","SWEPT_FACE",FACE,{"disambiguationData":[OSD([sQuery(id+"F13.wireOp",EDGE,"E218")])]}),makeQuery(id+"F14.opExtrude","SWEPT_FACE",FACE,{"disambiguationData":[OSD([sQuery(id+"F13.wireOp",EDGE,"E223")])]}),makeQuery(id+"F14.opExtrude","SWEPT_FACE",FACE,{"disambiguationData":[OSD([sQuery(id+"F13.wireOp",EDGE,"E228")])]}),makeQuery(id+"F14.opExtrude","SWEPT_FACE",FACE,{"disambiguationData":[OSD([sQuery(id+"F13.wireOp",EDGE,"E233")])]})]});
            var sketch = newSketch(context, id + "F17", { "sketchPlane" : qUnion([Q0])});
            skLineSegment(sketch, "E258", {"start": v(-301.42, 4) * mm, "end": v(-301.42, 2) * mm});
            skLineSegment(sketch, "E259", {"start": v(-301.42, 2) * mm, "end": v(-322.54, 2) * mm});
            skLineSegment(sketch, "E260", {"start": v(-322.54, 2) * mm, "end": v(-322.54, 4) * mm});
            skLineSegment(sketch, "E261", {"start": v(-322.54, 4) * mm, "end": v(-301.42, 4) * mm});
            skLineSegment(sketch, "E262", {"start": v(-322.23, 0) * mm, "end": v(-322.23, -2) * mm});
            skLineSegment(sketch, "E263", {"start": v(-322.23, -2) * mm, "end": v(-301.42, -2) * mm});
            skLineSegment(sketch, "E264", {"start": v(-301.42, -2) * mm, "end": v(-301.42, 0) * mm});
            skLineSegment(sketch, "E265", {"start": v(-301.42, 0) * mm, "end": v(-322.23, 0) * mm});
            skLineSegment(sketch, "E266", {"start": v(301.42, 0) * mm, "end": v(301.42, -2) * mm});
            skLineSegment(sketch, "E267", {"start": v(301.42, -2) * mm, "end": v(318.95, -2) * mm});
            skLineSegment(sketch, "E268", {"start": v(318.95, -2) * mm, "end": v(318.95, 0) * mm});
            skLineSegment(sketch, "E269", {"start": v(318.95, 0) * mm, "end": v(301.42, 0) * mm});
            skLineSegment(sketch, "E270", {"start": v(319.07, 4) * mm, "end": v(319.07, 2) * mm});
            skLineSegment(sketch, "E271", {"start": v(319.07, 2) * mm, "end": v(301.42, 2) * mm});
            skLineSegment(sketch, "E272", {"start": v(301.42, 2) * mm, "end": v(301.42, 4) * mm});
            skLineSegment(sketch, "E273", {"start": v(301.42, 4) * mm, "end": v(319.07, 4) * mm});
            skSolve(sketch);
        }
        {
            var Q0;
            Q0 = qSketchRegion(id + "F17", true);
            extrude(context, id + "F18", {"entities" : qUnion([Q0]), "operationType" : NewBodyOperationType.ADD, "depth" : 2 * mm, "offsetDistance" : 25 * mm});
        }
    });
